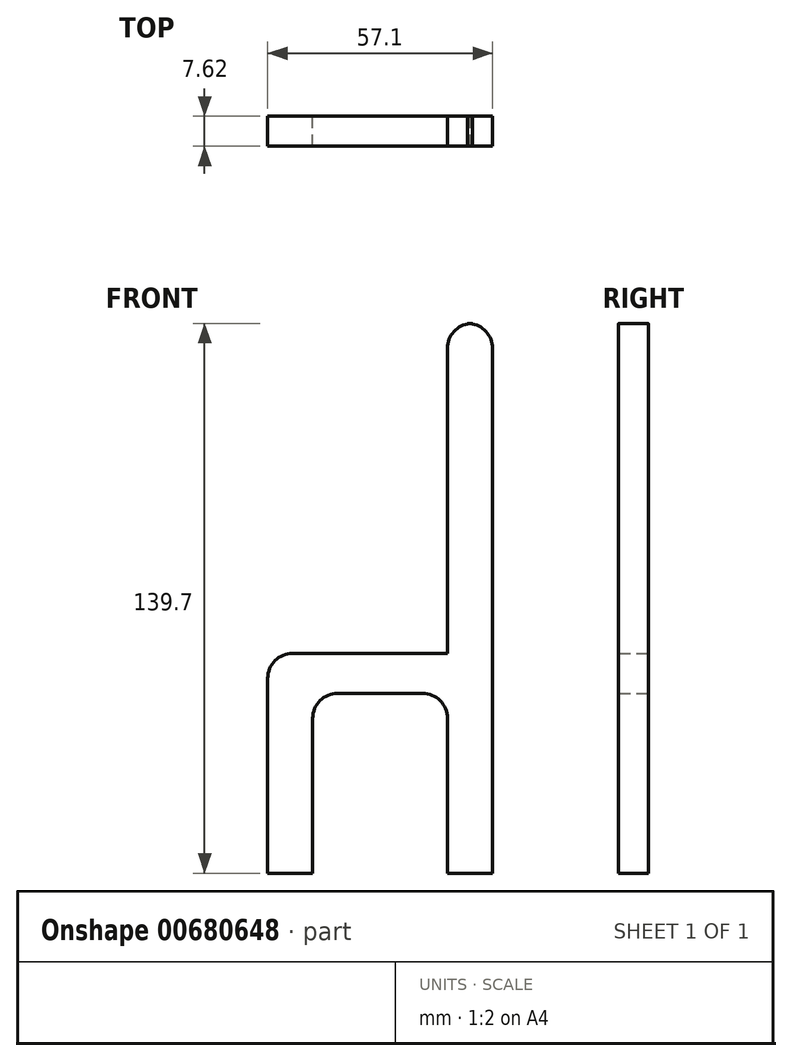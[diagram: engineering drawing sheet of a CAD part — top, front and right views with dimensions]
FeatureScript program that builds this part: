
annotation { "Feature Type Name" : "Feature", "Feature Type Description" : "" }
export const myFeature = defineFeature(function(context is Context, id is Id, definition is map)
    precondition{}
    {
        {
            var Q0;
            Q0=qCreatedBy(makeId("Front.planeOp"),FACE);
            var sketch = newSketch(context, id + "F0", { "sketchPlane" : qUnion([Q0])});
            skLineSegment(sketch, "E0", {"start": v(-52.34, -69.04) * mm, "end": v(-52.34, -19.51) * mm});
            skLineSegment(sketch, "E1", {"start": v(-46, -13.16) * mm, "end": v(-6.67, -13.16) * mm});
            skLineSegment(sketch, "E2", {"start": v(4.76, -13.16) * mm, "end": v(4.76, -69.04) * mm});
            skLineSegment(sketch, "E3", {"start": v(4.76, -13.16) * mm, "end": v(4.76, 64.3) * mm});
            skLineSegment(sketch, "E4", {"start": v(-52.34, -69.04) * mm, "end": v(-40.91, -69.04) * mm});
            skLineSegment(sketch, "E5", {"start": v(4.76, -69.04) * mm, "end": v(-6.67, -69.04) * mm});
            skLineSegment(sketch, "E6", {"start": v(-0.32, 70.66) * mm, "end": v(-1.6, 70.66) * mm});
            skLineSegment(sketch, "E7", {"start": v(-40.91, -69.04) * mm, "end": v(-40.91, -29.67) * mm});
            skLineSegment(sketch, "E8", {"start": v(-6.67, -69.04) * mm, "end": v(-6.67, -29.67) * mm});
            skLineSegment(sketch, "E9", {"start": v(-13.02, -23.32) * mm, "end": v(-34.56, -23.32) * mm});
            skLineSegment(sketch, "E10", {"start": v(-6.67, 64.3) * mm, "end": v(-6.67, -13.16) * mm});
            skPoint(sketch, "E11.visualSharp", {"position": v(-52.34, -13.16) * mm});
            skArc(sketch, "E11.filletArc", {"start": v(-46, -13.16) * mm, "mid": v(-50.48, -15.02) * mm, "end": v(-52.34, -19.51) * mm});
            skPoint(sketch, "E12.visualSharp", {"position": v(-6.67, 70.66) * mm});
            skArc(sketch, "E12.filletArc", {"start": v(-0.32, 70.66) * mm, "mid": v(-4.81, 68.8) * mm, "end": v(-6.67, 64.3) * mm});
            skPoint(sketch, "E13.visualSharp", {"position": v(4.76, 70.66) * mm});
            skArc(sketch, "E13.filletArc", {"start": v(4.76, 64.3) * mm, "mid": v(2.9, 68.8) * mm, "end": v(-1.6, 70.66) * mm});
            skPoint(sketch, "E14.visualSharp", {"position": v(-40.91, -23.32) * mm});
            skArc(sketch, "E14.filletArc", {"start": v(-34.56, -23.32) * mm, "mid": v(-39.05, -25.18) * mm, "end": v(-40.91, -29.67) * mm});
            skPoint(sketch, "E15.visualSharp", {"position": v(-6.67, -23.32) * mm});
            skArc(sketch, "E15.filletArc", {"start": v(-6.67, -29.67) * mm, "mid": v(-8.53, -25.18) * mm, "end": v(-13.02, -23.32) * mm});
            skSolve(sketch);
        }
        {
            var Q0;
            Q0 = qSketchRegion(id + "F0", true);
            extrude(context, id + "F1", {"entities" : qUnion([Q0]), "depth" : 7.62 * mm, "offsetDistance" : 25.4 * mm});
        }
    });
